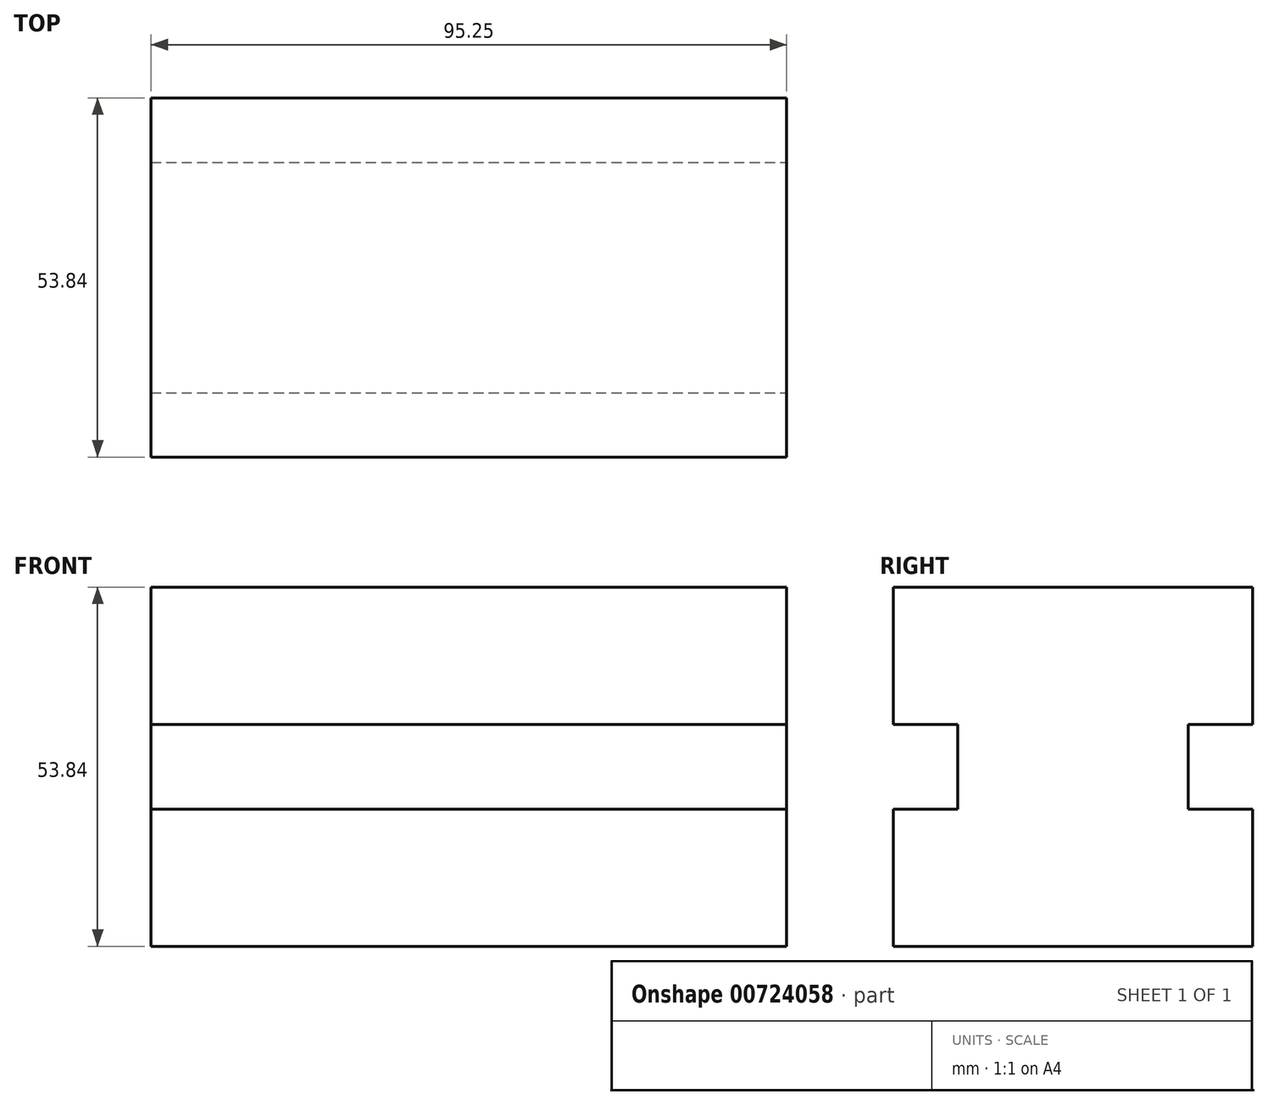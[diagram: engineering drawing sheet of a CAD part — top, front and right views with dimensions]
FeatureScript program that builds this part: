
annotation { "Feature Type Name" : "Feature", "Feature Type Description" : "" }
export const myFeature = defineFeature(function(context is Context, id is Id, definition is map)
    precondition{}
    {
        {
            var Q0;
            Q0=qCreatedBy(makeId("Right.planeOp"),FACE);
            var sketch = newSketch(context, id + "F0", { "sketchPlane" : qUnion([Q0])});
            skLineSegment(sketch, "E0.bottom", {"start": v(-26.92, 26.92) * mm, "end": v(26.92, 26.92) * mm});
            skLineSegment(sketch, "E0.top", {"start": v(-26.92, -26.92) * mm, "end": v(26.92, -26.92) * mm});
            skLineSegment(sketch, "E0.left", {"start": v(-26.92, 26.92) * mm, "end": v(-26.92, 6.35) * mm});
            skLineSegment(sketch, "E0.right", {"start": v(26.92, 26.92) * mm, "end": v(26.92, 6.35) * mm});
            skPoint(sketch, "E0.middle", {"position": v(0, 0) * mm});
            skLineSegment(sketch, "E1.bottom", {"start": v(-26.92, 6.35) * mm, "end": v(-17.27, 6.35) * mm});
            skLineSegment(sketch, "E1.top", {"start": v(-26.92, -6.35) * mm, "end": v(-17.27, -6.35) * mm});
            skLineSegment(sketch, "E1.right", {"start": v(-17.27, 6.35) * mm, "end": v(-17.27, -6.35) * mm});
            skLineSegment(sketch, "E2.trimOffspring", {"start": v(-26.92, -6.35) * mm, "end": v(-26.92, -26.92) * mm});
            skLineSegment(sketch, "E3", {"start": v(0, 31.7) * mm, "end": v(0, -34.2) * mm, "construction": true});
            skLineSegment(sketch, "E4.MirrorCS", {"start": v(26.92, 6.35) * mm, "end": v(17.27, 6.35) * mm});
            skLineSegment(sketch, "E5.MirrorCS", {"start": v(17.27, 6.35) * mm, "end": v(17.27, -6.35) * mm});
            skLineSegment(sketch, "E6.MirrorCS", {"start": v(26.92, -6.35) * mm, "end": v(17.27, -6.35) * mm});
            skLineSegment(sketch, "E7.trimOffspring", {"start": v(26.92, -6.35) * mm, "end": v(26.92, -26.92) * mm});
            skSolve(sketch);
        }
        {
            var Q0;
            Q0=makeQuery(id+"F0.imprint","IMPRINT",FACE,{"disambiguationData":[TD([[makeQuery(id+"F0.imprint","IMPRINT",EDGE,{"derivedFrom":sQuery(id+"F0.wireOp",EDGE,"E0.bottom")}),-1.0]])]});
            extrude(context, id + "F1", {"entities" : qUnion([Q0]), "oppositeDirection" : true, "depth" : 95.25 * mm, "offsetDistance" : 25.4 * mm});
        }
    });
